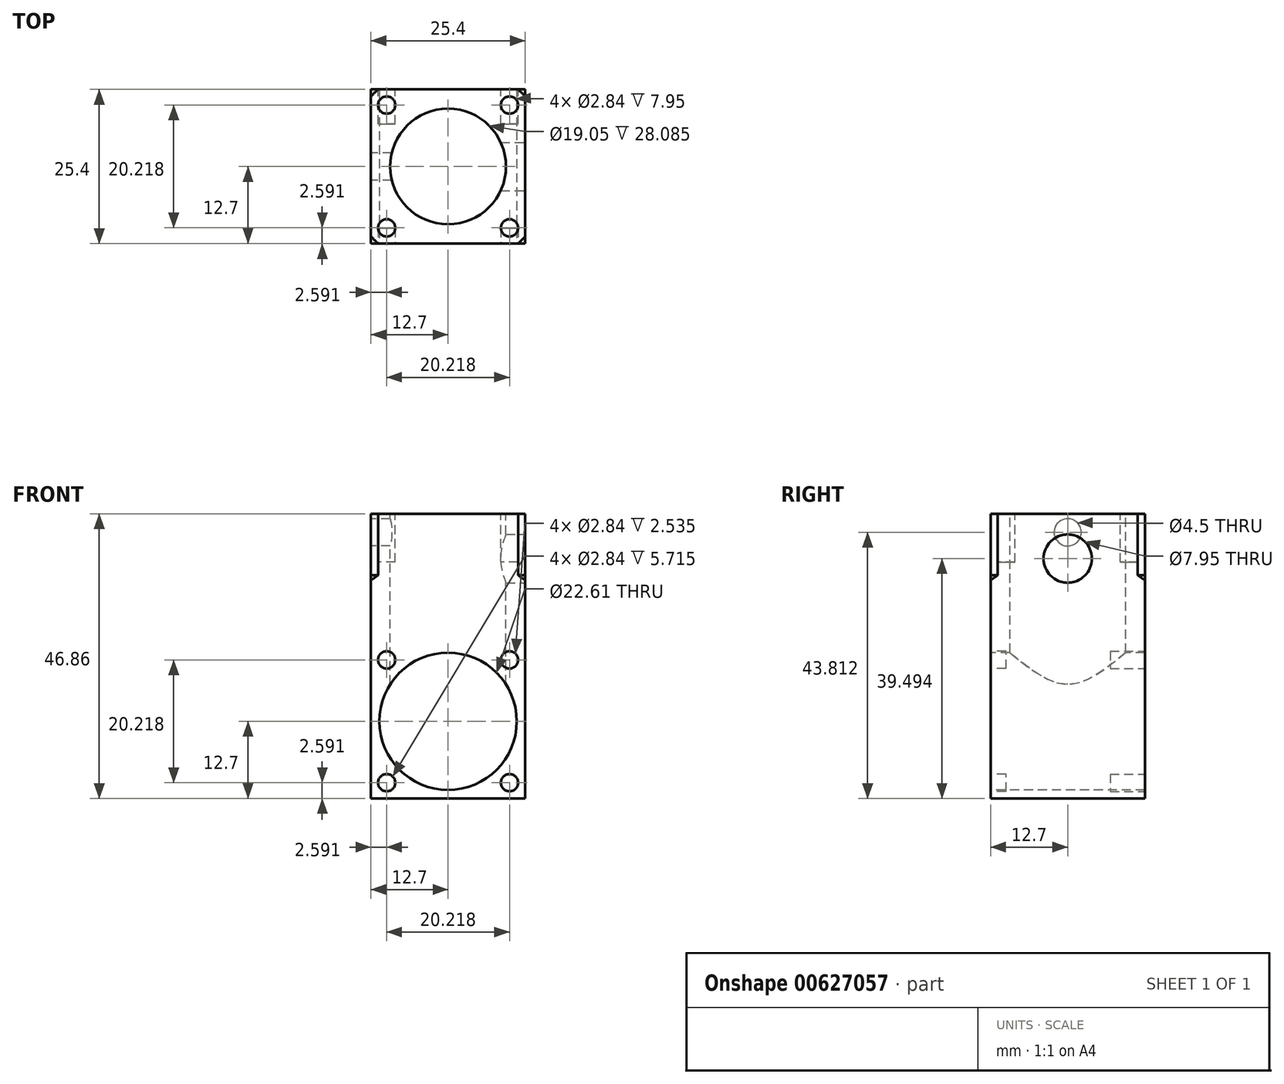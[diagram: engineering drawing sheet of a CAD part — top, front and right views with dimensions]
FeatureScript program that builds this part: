
annotation { "Feature Type Name" : "Feature", "Feature Type Description" : "" }
export const myFeature = defineFeature(function(context is Context, id is Id, definition is map)
    precondition{}
    {
        {
            var Q0;
            Q0=qCreatedBy(makeId("Top.planeOp"),FACE);
            var sketch = newSketch(context, id + "F0", { "sketchPlane" : qUnion([Q0])});
            skLineSegment(sketch, "E0.bottom", {"start": v(12.7, -12.7) * mm, "end": v(-12.7, -12.7) * mm});
            skLineSegment(sketch, "E0.top", {"start": v(12.7, 12.7) * mm, "end": v(-12.7, 12.7) * mm});
            skLineSegment(sketch, "E0.left", {"start": v(12.7, -12.7) * mm, "end": v(12.7, 12.7) * mm});
            skLineSegment(sketch, "E0.right", {"start": v(-12.7, -12.7) * mm, "end": v(-12.7, 12.7) * mm});
            skPoint(sketch, "E0.middle", {"position": v(0, 0) * mm});
            skSolve(sketch);
        }
        {
            var Q0;
            Q0=makeQuery(id+"F0.imprint","IMPRINT",FACE,{"disambiguationData":[TD([[makeQuery(id+"F0.imprint","IMPRINT",EDGE,{"derivedFrom":sQuery(id+"F0.wireOp",EDGE,"E0.bottom")}),-1.0]])]});
            extrude(context, id + "F1", {"entities" : qUnion([Q0]), "depth" : 46.86 * mm, "offsetDistance" : 25 * mm});
        }
        {
            var Q0;
            Q0=makeQuery(id+"F1.opExtrude","CAP_FACE",FACE,{"disambiguationData":[OSD([sQuery(id+"F0.wireOp",EDGE,"E0.bottom"),sQuery(id+"F0.wireOp",EDGE,"E0.top"),sQuery(id+"F0.wireOp",EDGE,"E0.left"),sQuery(id+"F0.wireOp",EDGE,"E0.right")])],"isStart":false});
            var sketch = newSketch(context, id + "F2", { "sketchPlane" : qUnion([Q0])});
            skArc(sketch, "E1", {"start": v(-10.31, 13.7) * mm, "mid": v(-13.65, 10.37) * mm, "end": v(-15.95, 6.27) * mm});
            skLineSegment(sketch, "E2", {"start": v(-10.31, 13.7) * mm, "end": v(-15.95, 13.7) * mm});
            skLineSegment(sketch, "E3", {"start": v(-15.95, 13.7) * mm, "end": v(-15.95, 6.27) * mm});
            skLineSegment(sketch, "E4", {"start": v(-14.87, -8.52) * mm, "end": v(-14.87, -15.51) * mm});
            skLineSegment(sketch, "E5", {"start": v(-14.87, -15.51) * mm, "end": v(-7.29, -15.51) * mm});
            skLineSegment(sketch, "E6", {"start": v(14.32, -9.42) * mm, "end": v(14.32, -16.49) * mm});
            skLineSegment(sketch, "E7", {"start": v(14.32, -16.49) * mm, "end": v(4.68, -16.49) * mm});
            skLineSegment(sketch, "E8", {"start": v(8.55, 14.85) * mm, "end": v(15.32, 14.85) * mm});
            skLineSegment(sketch, "E9", {"start": v(15.32, 14.85) * mm, "end": v(15.32, 7.68) * mm});
            skArc(sketch, "E10.trimOffspring", {"start": v(-14.87, -8.52) * mm, "mid": v(-11.62, -12.6) * mm, "end": v(-7.29, -15.51) * mm});
            skArc(sketch, "E11.trimOffspring", {"start": v(4.68, -16.49) * mm, "mid": v(10.14, -13.82) * mm, "end": v(14.32, -9.42) * mm});
            skArc(sketch, "E12.trimOffspring", {"start": v(15.32, 7.68) * mm, "mid": v(12.46, 11.76) * mm, "end": v(8.55, 14.85) * mm});
            skSolve(sketch);
        }
        {
            var Q0;
            {var subQ0=sQuery(id+"F2.wireOp",EDGE,"E10.trimOffspring");var subQ1=makeQuery(id+"F1.opExtrude","CAP_EDGE",EDGE,{"disambiguationData":[OSD([sQuery(id+"F0.wireOp",EDGE,"E0.right")])],"isStart":false});var subQ2=makeQuery(id+"F2.imprint","INTERSECT",VERTEX,{"derivedFrom":[subQ1,subQ0]});Q0=makeQuery(id+"F2.imprint","IMPRINT",FACE,{"disambiguationData":[TD([[makeQuery(id+"F2.imprint","IMPRINT",EDGE,{"disambiguationData":[TD([[subQ2,-1.0]])],"derivedFrom":subQ0}),-1.0]])]});}
            var Q1;
            {var subQ0=sQuery(id+"F2.wireOp",EDGE,"E1");var subQ1=makeQuery(id+"F1.opExtrude","CAP_EDGE",EDGE,{"disambiguationData":[OSD([sQuery(id+"F0.wireOp",EDGE,"E0.top")])],"isStart":false});var subQ2=makeQuery(id+"F2.imprint","INTERSECT",VERTEX,{"derivedFrom":[subQ1,subQ0]});Q1=makeQuery(id+"F2.imprint","IMPRINT",FACE,{"disambiguationData":[TD([[makeQuery(id+"F2.imprint","IMPRINT",EDGE,{"disambiguationData":[TD([[subQ2,-1.0]])],"derivedFrom":subQ0}),-1.0]])]});}
            var Q2;
            {var subQ0=sQuery(id+"F2.wireOp",EDGE,"E12.trimOffspring");var subQ1=makeQuery(id+"F1.opExtrude","CAP_EDGE",EDGE,{"disambiguationData":[OSD([sQuery(id+"F0.wireOp",EDGE,"E0.left")])],"isStart":false});var subQ2=makeQuery(id+"F2.imprint","INTERSECT",VERTEX,{"derivedFrom":[subQ1,subQ0]});Q2=makeQuery(id+"F2.imprint","IMPRINT",FACE,{"disambiguationData":[TD([[makeQuery(id+"F2.imprint","IMPRINT",EDGE,{"disambiguationData":[TD([[subQ2,-1.0]])],"derivedFrom":subQ0}),-1.0]])]});}
            var Q3;
            {var subQ0=sQuery(id+"F2.wireOp",EDGE,"E11.trimOffspring");var subQ1=makeQuery(id+"F1.opExtrude","CAP_EDGE",EDGE,{"disambiguationData":[OSD([sQuery(id+"F0.wireOp",EDGE,"E0.bottom")])],"isStart":false});var subQ2=makeQuery(id+"F2.imprint","INTERSECT",VERTEX,{"derivedFrom":[subQ1,subQ0]});Q3=makeQuery(id+"F2.imprint","IMPRINT",FACE,{"disambiguationData":[TD([[makeQuery(id+"F2.imprint","IMPRINT",EDGE,{"disambiguationData":[TD([[subQ2,-1.0]])],"derivedFrom":subQ0}),-1.0]])]});}
            extrude(context, id + "F3", {"entities" : qUnion([Q0, Q1, Q2, Q3]), "operationType" : NewBodyOperationType.REMOVE, "oppositeDirection" : true, "depth" : 11.1 * mm, "offsetDistance" : 25 * mm});
        }
        {
            var Q0;
            Q0=makeQuery(id+"F3.boolean.opBoolean","COPY",EDGE,{"derivedFrom":makeQuery(id+"F3.opExtrude","CAP_EDGE",EDGE,{"disambiguationData":[OSD([sQuery(id+"F2.wireOp",EDGE,"E10.trimOffspring")])],"isStart":false})});
            var Q1;
            Q1=makeQuery(id+"F3.boolean.opBoolean","COPY",EDGE,{"derivedFrom":makeQuery(id+"F3.opExtrude","CAP_EDGE",EDGE,{"disambiguationData":[OSD([sQuery(id+"F2.wireOp",EDGE,"E11.trimOffspring")])],"isStart":false})});
            var Q2;
            Q2=makeQuery(id+"F3.boolean.opBoolean","COPY",EDGE,{"derivedFrom":makeQuery(id+"F3.opExtrude","CAP_EDGE",EDGE,{"disambiguationData":[OSD([sQuery(id+"F2.wireOp",EDGE,"E12.trimOffspring")])],"isStart":false})});
            var Q3;
            Q3=makeQuery(id+"F3.boolean.opBoolean","COPY",EDGE,{"derivedFrom":makeQuery(id+"F3.opExtrude","CAP_EDGE",EDGE,{"disambiguationData":[OSD([sQuery(id+"F2.wireOp",EDGE,"E1")])],"isStart":false})});
            chamfer(context, id + "F4", {"entities" : qUnion([Q0, Q1, Q2, Q3]), "width" : 1 * mm, "tangentPropagation" : true});
        }
        {
            var Q0;
            Q0=makeQuery(id+"F1.opExtrude","SWEPT_FACE",FACE,{"disambiguationData":[OSD([sQuery(id+"F0.wireOp",EDGE,"E0.right")])]});
            var sketch = newSketch(context, id + "F5", { "sketchPlane" : qUnion([Q0])});
            skCircle(sketch, "E13", {"center": v(0, 43.81) * mm, "radius": 2.25 * mm});
            skSolve(sketch);
        }
        {
            var Q0;
            Q0 = qSketchRegion(id + "F5", true);
            extrude(context, id + "F6", {"entities" : qUnion([Q0]), "operationType" : NewBodyOperationType.REMOVE, "oppositeDirection" : true, "depth" : 6.44 * mm, "offsetDistance" : 25.4 * mm});
        }
        {
            var Q0;
            Q0=makeQuery(id+"F1.opExtrude","SWEPT_FACE",FACE,{"disambiguationData":[OSD([sQuery(id+"F0.wireOp",EDGE,"E0.bottom")])]});
            var sketch = newSketch(context, id + "F7", { "sketchPlane" : qUnion([Q0])});
            skCircle(sketch, "E14", {"center": v(0, 12.7) * mm, "radius": 11.3 * mm});
            skCircle(sketch, "E15", {"center": v(10.1, 22.8) * mm, "radius": 1.42 * mm});
            skCircle(sketch, "E16", {"center": v(10.1, 2.6) * mm, "radius": 1.42 * mm});
            skCircle(sketch, "E17", {"center": v(-10.1, 2.6) * mm, "radius": 1.42 * mm});
            skCircle(sketch, "E18", {"center": v(-10.1, 22.8) * mm, "radius": 1.42 * mm});
            skSolve(sketch);
        }
        {
            var Q0;
            Q0=makeQuery(id+"F1.opExtrude","CAP_FACE",FACE,{"disambiguationData":[OSD([sQuery(id+"F0.wireOp",EDGE,"E0.bottom"),sQuery(id+"F0.wireOp",EDGE,"E0.top"),sQuery(id+"F0.wireOp",EDGE,"E0.left"),sQuery(id+"F0.wireOp",EDGE,"E0.right")])],"isStart":false});
            var sketch = newSketch(context, id + "F8", { "sketchPlane" : qUnion([Q0])});
            skCircle(sketch, "E19", {"center": v(0, 0) * mm, "radius": 9.53 * mm});
            skSolve(sketch);
        }
        {
            var Q0;
            Q0=makeQuery(id+"F8.imprint","IMPRINT",FACE,{"disambiguationData":[TD([[makeQuery(id+"F8.imprint","IMPRINT",EDGE,{"derivedFrom":sQuery(id+"F8.wireOp",EDGE,"E19")}),1.0]])]});
            extrude(context, id + "F9", {"entities" : qUnion([Q0]), "operationType" : NewBodyOperationType.REMOVE, "oppositeDirection" : true, "depth" : 31.75 * mm, "offsetDistance" : 25.4 * mm});
        }
        {
            var Q0;
            Q0=makeQuery(id+"F1.opExtrude","CAP_FACE",FACE,{"disambiguationData":[OSD([sQuery(id+"F0.wireOp",EDGE,"E0.bottom"),sQuery(id+"F0.wireOp",EDGE,"E0.top"),sQuery(id+"F0.wireOp",EDGE,"E0.left"),sQuery(id+"F0.wireOp",EDGE,"E0.right")])],"isStart":false});
            var sketch = newSketch(context, id + "F10", { "sketchPlane" : qUnion([Q0])});
            skCircle(sketch, "E20", {"center": v(10.1, 10.1) * mm, "radius": 1.42 * mm});
            skCircle(sketch, "E21", {"center": v(10.1, -10.1) * mm, "radius": 1.42 * mm});
            skCircle(sketch, "E22", {"center": v(-10.1, -10.1) * mm, "radius": 1.42 * mm});
            skCircle(sketch, "E23", {"center": v(-10.1, 10.1) * mm, "radius": 1.42 * mm});
            skSolve(sketch);
        }
        {
            var Q0;
            Q0=makeQuery(id+"F10.imprint","IMPRINT",FACE,{"disambiguationData":[TD([[makeQuery(id+"F10.imprint","IMPRINT",EDGE,{"derivedFrom":sQuery(id+"F10.wireOp",EDGE,"E21")}),1.0]])]});
            var Q1;
            Q1=makeQuery(id+"F10.imprint","IMPRINT",FACE,{"disambiguationData":[TD([[makeQuery(id+"F10.imprint","IMPRINT",EDGE,{"derivedFrom":sQuery(id+"F10.wireOp",EDGE,"E20")}),1.0]])]});
            var Q2;
            Q2=makeQuery(id+"F10.imprint","IMPRINT",FACE,{"disambiguationData":[TD([[makeQuery(id+"F10.imprint","IMPRINT",EDGE,{"derivedFrom":sQuery(id+"F10.wireOp",EDGE,"E23")}),1.0]])]});
            var Q3;
            Q3=makeQuery(id+"F10.imprint","IMPRINT",FACE,{"disambiguationData":[TD([[makeQuery(id+"F10.imprint","IMPRINT",EDGE,{"derivedFrom":sQuery(id+"F10.wireOp",EDGE,"E22")}),1.0]])]});
            extrude(context, id + "F11", {"entities" : qUnion([Q0, Q1, Q2, Q3]), "operationType" : NewBodyOperationType.REMOVE, "oppositeDirection" : true, "depth" : 7.95 * mm, "offsetDistance" : 25.4 * mm});
        }
        {
            var Q0;
            Q0=makeQuery(id+"F7.imprint","IMPRINT",FACE,{"disambiguationData":[TD([[makeQuery(id+"F7.imprint","IMPRINT",EDGE,{"derivedFrom":sQuery(id+"F7.wireOp",EDGE,"E14")}),1.0]])]});
            extrude(context, id + "F12", {"entities" : qUnion([Q0]), "operationType" : NewBodyOperationType.REMOVE, "endBound" : BoundingType.THROUGH_ALL, "oppositeDirection" : true, "depth" : 25.4 * mm, "offsetDistance" : 25.4 * mm});
        }
        {
            var Q0;
            Q0=makeQuery(id+"F7.imprint","IMPRINT",FACE,{"disambiguationData":[TD([[makeQuery(id+"F7.imprint","IMPRINT",EDGE,{"derivedFrom":sQuery(id+"F7.wireOp",EDGE,"E15")}),1.0]])]});
            var Q1;
            Q1=makeQuery(id+"F7.imprint","IMPRINT",FACE,{"disambiguationData":[TD([[makeQuery(id+"F7.imprint","IMPRINT",EDGE,{"derivedFrom":sQuery(id+"F7.wireOp",EDGE,"E16")}),1.0]])]});
            var Q2;
            Q2=makeQuery(id+"F7.imprint","IMPRINT",FACE,{"disambiguationData":[TD([[makeQuery(id+"F7.imprint","IMPRINT",EDGE,{"derivedFrom":sQuery(id+"F7.wireOp",EDGE,"E17")}),1.0]])]});
            var Q3;
            Q3=makeQuery(id+"F7.imprint","IMPRINT",FACE,{"disambiguationData":[TD([[makeQuery(id+"F7.imprint","IMPRINT",EDGE,{"derivedFrom":sQuery(id+"F7.wireOp",EDGE,"E18")}),1.0]])]});
            extrude(context, id + "F13", {"entities" : qUnion([Q0, Q1, Q2, Q3]), "operationType" : NewBodyOperationType.REMOVE, "oppositeDirection" : true, "depth" : 2.53 * mm, "offsetDistance" : 25.4 * mm});
        }
        {
            var Q0;
            Q0=makeQuery(id+"F1.opExtrude","SWEPT_FACE",FACE,{"disambiguationData":[OSD([sQuery(id+"F0.wireOp",EDGE,"E0.left")])]});
            var sketch = newSketch(context, id + "F14", { "sketchPlane" : qUnion([Q0])});
            skCircle(sketch, "E24", {"center": v(0, 39.5) * mm, "radius": 3.98 * mm});
            skSolve(sketch);
        }
        {
            var Q0;
            Q0 = qSketchRegion(id + "F14", true);
            extrude(context, id + "F15", {"entities" : qUnion([Q0]), "operationType" : NewBodyOperationType.REMOVE, "oppositeDirection" : true, "depth" : 6.35 * mm, "offsetDistance" : 25.4 * mm});
        }
        {
            var Q0;
            Q0=makeQuery(id+"F1.opExtrude","SWEPT_FACE",FACE,{"disambiguationData":[OSD([sQuery(id+"F0.wireOp",EDGE,"E0.top")])]});
            var sketch = newSketch(context, id + "F16", { "sketchPlane" : qUnion([Q0])});
            skCircle(sketch, "E25.0", {"center": v(10.1, 22.8) * mm, "radius": 1.42 * mm});
            skCircle(sketch, "E26.0", {"center": v(-10.1, 22.8) * mm, "radius": 1.42 * mm});
            skCircle(sketch, "E27.0", {"center": v(-10.1, 2.6) * mm, "radius": 1.42 * mm});
            skCircle(sketch, "E28.0", {"center": v(10.1, 2.6) * mm, "radius": 1.42 * mm});
            skSolve(sketch);
        }
        {
            var Q0;
            Q0=makeQuery(id+"F16.imprint","IMPRINT",FACE,{"disambiguationData":[TD([[makeQuery(id+"F16.imprint","IMPRINT",EDGE,{"derivedFrom":sQuery(id+"F16.wireOp",EDGE,"E26.0")}),1.0]])]});
            var Q1;
            Q1=makeQuery(id+"F16.imprint","IMPRINT",FACE,{"disambiguationData":[TD([[makeQuery(id+"F16.imprint","IMPRINT",EDGE,{"derivedFrom":sQuery(id+"F16.wireOp",EDGE,"E25.0")}),1.0]])]});
            var Q2;
            Q2=makeQuery(id+"F16.imprint","IMPRINT",FACE,{"disambiguationData":[TD([[makeQuery(id+"F16.imprint","IMPRINT",EDGE,{"derivedFrom":sQuery(id+"F16.wireOp",EDGE,"E28.0")}),1.0]])]});
            var Q3;
            Q3=makeQuery(id+"F16.imprint","IMPRINT",FACE,{"disambiguationData":[TD([[makeQuery(id+"F16.imprint","IMPRINT",EDGE,{"derivedFrom":sQuery(id+"F16.wireOp",EDGE,"E27.0")}),1.0]])]});
            extrude(context, id + "F17", {"entities" : qUnion([Q0, Q1, Q2, Q3]), "operationType" : NewBodyOperationType.REMOVE, "oppositeDirection" : true, "depth" : 5.7 * mm, "offsetDistance" : 25.4 * mm});
        }
    });
